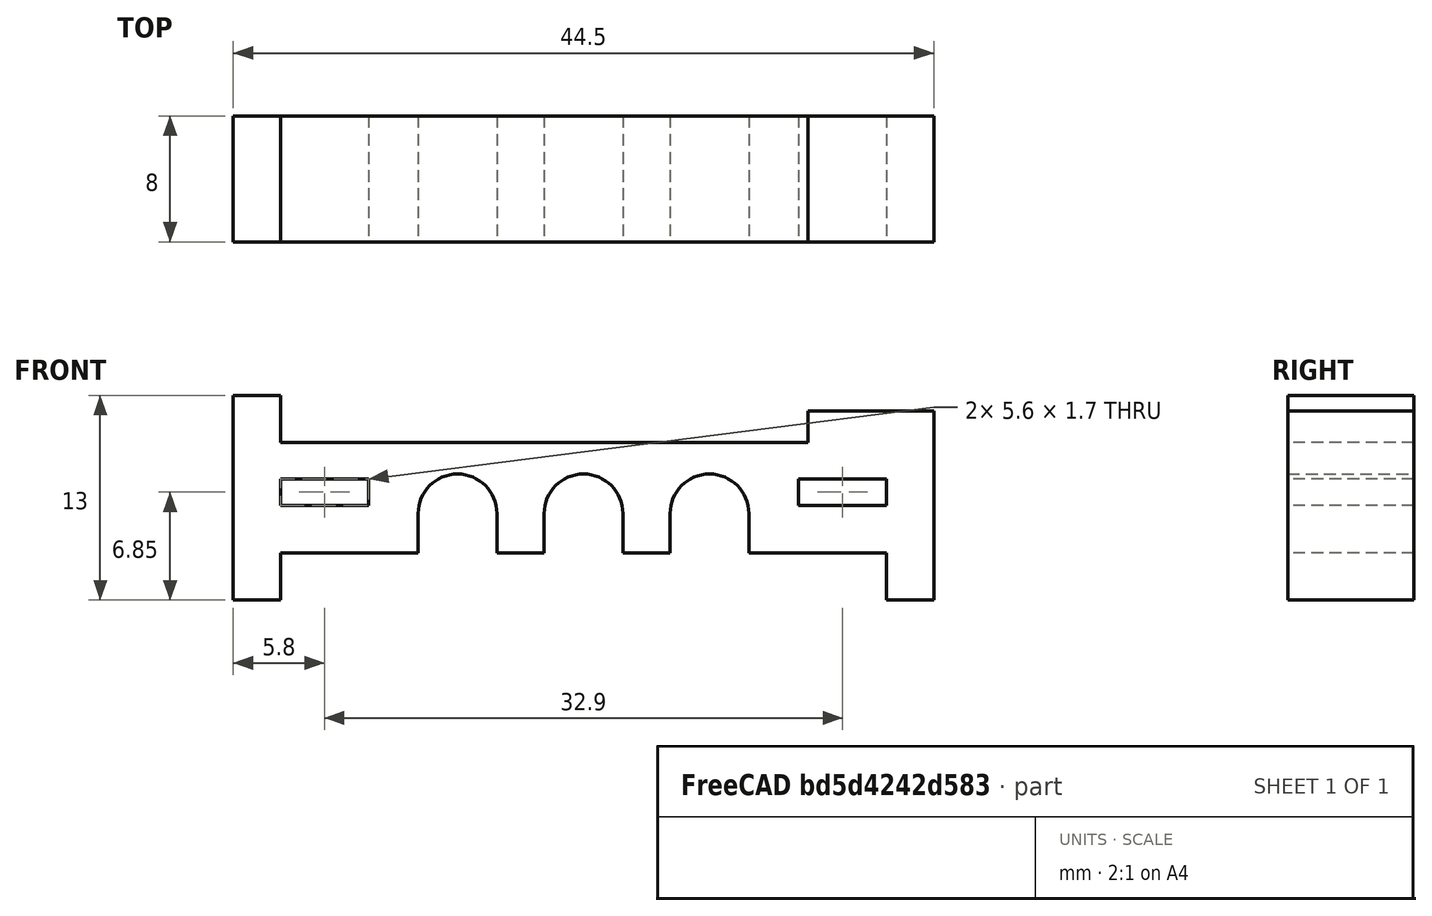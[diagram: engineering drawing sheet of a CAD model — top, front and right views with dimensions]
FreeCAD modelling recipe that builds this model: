
FCSTD DOCUMENT  (FreeCAD 0.19R24366 (Git))
Label: soundsupport
License: All rights reserved
LicenseURL: http://en.wikipedia.org/wiki/All_rights_reserved
objects: Sketcher::SketchObject×2, PartDesign::Pad×1, PartDesign::Body×1, Part::Part2DObjectPython×1
note: 6 computed .brp shape members not serialized (recipe doc carries the construction recipe); baked Part::Feature solids carry a one-line shape summary decoded from their .brp

FEATURE [Sketcher::SketchObject] Sketch
  FullyConstrained = true
  MapMode = 5
  Placement = pos=(0,0,0) rot=(1,0,0;1.5708rad)
  Support = -> [XZ_Plane]
  expr: Constraints[71] = .Constraints.radius
  sketch-geometry (32):
    g0: LineSegment StartX=-22.25 StartY=-3 StartZ=0 EndX=-19.25 EndY=-3 EndZ=0
    g1: LineSegment StartX=-19.25 StartY=-3 StartZ=0 EndX=-19.25 EndY=0 EndZ=0
    g2: LineSegment StartX=-19.25 StartY=0 StartZ=0 EndX=-10.5 EndY=0 EndZ=0
    g3: LineSegment StartX=-10.5 StartY=0 StartZ=0 EndX=-10.5 EndY=2.5 EndZ=0
    g4: LineSegment StartX=-5.5 StartY=2.5 StartZ=0 EndX=-5.5 EndY=0 EndZ=0
    g5: LineSegment StartX=-5.5 StartY=0 StartZ=0 EndX=-2.5 EndY=0 EndZ=0
    g6: LineSegment StartX=-2.5 StartY=0 StartZ=0 EndX=-2.5 EndY=2.5 EndZ=0
    g7: LineSegment StartX=2.5 StartY=2.5 StartZ=0 EndX=2.5 EndY=0 EndZ=0
    g8: LineSegment StartX=2.5 StartY=0 StartZ=0 EndX=5.5 EndY=0 EndZ=0
    g9: LineSegment StartX=5.5 StartY=0 StartZ=0 EndX=5.5 EndY=2.5 EndZ=0
    g10: LineSegment StartX=10.5 StartY=2.5 StartZ=0 EndX=10.5 EndY=0 EndZ=0
    g11: LineSegment StartX=10.5 StartY=0 StartZ=0 EndX=19.25 EndY=0 EndZ=0
    g12: LineSegment StartX=19.25 StartY=0 StartZ=0 EndX=19.25 EndY=-3 EndZ=0
    g13: LineSegment StartX=19.25 StartY=-3 StartZ=0 EndX=22.25 EndY=-3 EndZ=0
    g14: LineSegment StartX=22.25 StartY=-3 StartZ=0 EndX=22.25 EndY=9 EndZ=0
    g15: LineSegment StartX=22.25 StartY=9 StartZ=0 EndX=14.25 EndY=9 EndZ=0
    g16: LineSegment StartX=14.25 StartY=9 StartZ=0 EndX=14.25 EndY=7 EndZ=0
    g17: LineSegment StartX=14.25 StartY=7 StartZ=0 EndX=-19.25 EndY=7 EndZ=0
    g18: LineSegment StartX=-19.25 StartY=7 StartZ=0 EndX=-19.25 EndY=10 EndZ=0
    g19: LineSegment StartX=-19.25 StartY=10 StartZ=0 EndX=-22.25 EndY=10 EndZ=0
    g20: LineSegment StartX=-22.25 StartY=10 StartZ=0 EndX=-22.25 EndY=-3 EndZ=0
    g21: ArcOfCircle CenterX=-8 CenterY=2.5 CenterZ=0 NormalX=0 NormalY=0 NormalZ=1 AngleXU=0 Radius=2.5 StartAngle=3.48467e-08 EndAngle=3.14159
    g22: ArcOfCircle CenterX=-1.3e-15 CenterY=2.5 CenterZ=0 NormalX=0 NormalY=0 NormalZ=1 AngleXU=0 Radius=2.5 StartAngle=8.31012e-09 EndAngle=3.14159
    g23: ArcOfCircle CenterX=8 CenterY=2.5 CenterZ=0 NormalX=0 NormalY=0 NormalZ=1 AngleXU=0 Radius=2.5 StartAngle=6.28319 EndAngle=9.42478
    g24: LineSegment StartX=-19.25 StartY=4.7 StartZ=0 EndX=-13.65 EndY=4.7 EndZ=0
    g25: LineSegment StartX=-13.65 StartY=4.7 StartZ=0 EndX=-13.65 EndY=3 EndZ=0
    g26: LineSegment StartX=-13.65 StartY=3 StartZ=0 EndX=-19.25 EndY=3 EndZ=0
    g27: LineSegment StartX=-19.25 StartY=3 StartZ=0 EndX=-19.25 EndY=4.7 EndZ=0
    g28: LineSegment StartX=13.65 StartY=4.7 StartZ=0 EndX=19.25 EndY=4.7 EndZ=0
    g29: LineSegment StartX=19.25 StartY=4.7 StartZ=0 EndX=19.25 EndY=3 EndZ=0
    g30: LineSegment StartX=19.25 StartY=3 StartZ=0 EndX=13.65 EndY=3 EndZ=0
    g31: LineSegment StartX=13.65 StartY=3 StartZ=0 EndX=13.65 EndY=4.7 EndZ=0
  constraints (98):
    c: Horizontal(g0)
    c: Coincident(g0,g1)
    c: Vertical(g1)
    c: Coincident(g1,g2)
    c: Horizontal(g2)
    c: Coincident(g2,g3)
    c: Vertical(g3)
    c: Vertical(g4)
    c: Coincident(g4,g5)
    c: Horizontal(g5)
    c: Coincident(g5,g6)
    c: Vertical(g6)
    c: Vertical(g7)
    c: Coincident(g7,g8)
    c: Horizontal(g8)
    c: Coincident(g8,g9)
    c: Vertical(g9)
    c: Vertical(g10)
    c: Coincident(g10,g11)
    c: Horizontal(g11)
    c: Coincident(g11,g12)
    c: Vertical(g12)
    c: Coincident(g12,g13)
    c: Horizontal(g13)
    c: Coincident(g13,g14)
    c: Vertical(g14)
    c: Coincident(g14,g15)
    c: Horizontal(g15)
    c: Coincident(g15,g16)
    c: Coincident(g16,g17)
    c: Horizontal(g17)
    c: Coincident(g17,g18)
    c: Vertical(g18)
    c: Coincident(g18,g19)
    c: Horizontal(g19)
    c: Coincident(g19,g20)
    c: Coincident(g20,g0)
    c: Vertical(g20)
    c: Vertical(g16)
    c: Equal(g0,g1)
    c: Equal(g1,g12)
    c: Equal(g12,g13)
    c: DistanceX(g0,g0) = 3
    c: Equal(g3,g4)
    c: Equal(g4,g6)
    c: Equal(g6,g7)
    c: Equal(g7,g9)
    c: Equal(g9,g10)
    c: DistanceY(g3,g3) = 2.5  'radius'
    c: DistanceX(g17,g17) = 33.5
    c: DistanceX(g15,g15) = 8
    c: DistanceY(g16,g16) = 2
    c: DistanceY(g18,g18) = 3
    c: DistanceY(g11,g14) = 9
    c: Horizontal(g0,g12)
    c: Horizontal(g4,g2)
    c: Horizontal(g7,g10)
    c: Equal(g18,g19)
    c: Equal(g5,g8)
    c: DistanceX(g5,g5) = 3
    c: Coincident(g21,g4)
    c: Coincident(g21,g3)
    c: Coincident(g22,g7)
    c: Coincident(g22,g6)
    c: Coincident(g23,g10)
    c: Coincident(g23,g9)
    c: Tangent(g21,g3)
    c: Tangent(g22,g6)
    c: Tangent(g23,g9)
    c: Equal(g21,g22)
    c: Equal(g22,g23)
    c: Radius(g21) = 2.5
    c: Equal(g2,g11)
    c: Symmetric(g11,g1,g-1)
    c: Coincident(g24,g25)
    c: Coincident(g25,g26)
    c: Coincident(g26,g27)
    c: Coincident(g27,g24)
    c: Horizontal(g24)
    c: Horizontal(g26)
    c: Vertical(g25)
    c: Vertical(g27)
    c: Coincident(g28,g29)
    c: Coincident(g29,g30)
    c: Coincident(g30,g31)
    c: Coincident(g31,g28)
    c: Horizontal(g28)
    c: Horizontal(g30)
    c: Vertical(g29)
    c: Vertical(g31)
    c: Equal(g27,g31)
    c: Equal(g24,g28)
    c: DistanceY(g27,g27) = 1.7
    c: DistanceX(g24,g24) = 5.6
    c: Vertical(g1,g26)
    c: Vertical(g11,g29)
    c: DistanceY(g1,g26) = 3
    c: Horizontal(g30,g25)
FEATURE [PartDesign::Pad] Pad
  Direction = (1,1,1)
  Length = 8
  Length2 = 100
  Placement = pos=(0,0,0) rot=(1,0,0;1.5708rad)
  Profile = -> Sketch
  Refine = true
  Type = 0
FEATURE [PartDesign::Body] Body
  Group = -> [Sketch,Pad]
  Origin = -> Origin
  Tip = -> Pad
FEATURE [Part::Part2DObjectPython] Shape2DView  # Draft 2D object (typed FeaturePython)
  Base = -> Pad
  FaceNumbers = [33]
  FuseArch = false
  HiddenLines = false
  InPlace = true
  Projection = (0,-1,0)
  ProjectionMode = 0
  SegmentLength = 0.05
  Tessellation = false
  VisibleOnly = false
FEATURE [Sketcher::SketchObject] Sketch001  label="soundsupport"
  FullyConstrained = false
  sketch-geometry (32):
    g0: LineSegment StartX=-2.5 StartY=10.5 StartZ=0 EndX=-4.9e-15 EndY=10.5 EndZ=0
    g1: LineSegment StartX=-5.3e-15 StartY=10.5 StartZ=0 EndX=-5.3e-15 EndY=19.25 EndZ=0
    g2: LineSegment StartX=-5.3e-15 StartY=19.25 StartZ=0 EndX=3 EndY=19.25 EndZ=0
    g3: LineSegment StartX=3 StartY=19.25 StartZ=0 EndX=3 EndY=22.25 EndZ=0
    g4: LineSegment StartX=3 StartY=22.25 StartZ=0 EndX=-9 EndY=22.25 EndZ=0
    g5: LineSegment StartX=-9 StartY=22.25 StartZ=0 EndX=-9 EndY=14.25 EndZ=0
    g6: LineSegment StartX=-9 StartY=14.25 StartZ=0 EndX=-7 EndY=14.25 EndZ=0
    g7: LineSegment StartX=-7 StartY=14.25 StartZ=0 EndX=-7 EndY=-19.25 EndZ=0
    g8: LineSegment StartX=-7 StartY=-19.25 StartZ=0 EndX=-10 EndY=-19.25 EndZ=0
    g9: LineSegment StartX=-10 StartY=-19.25 StartZ=0 EndX=-10 EndY=-22.25 EndZ=0
    g10: LineSegment StartX=-10 StartY=-22.25 StartZ=0 EndX=3 EndY=-22.25 EndZ=0
    g11: LineSegment StartX=3 StartY=-22.25 StartZ=0 EndX=3 EndY=-19.25 EndZ=0
    g12: LineSegment StartX=3 StartY=-19.25 StartZ=0 EndX=-5.8e-15 EndY=-19.25 EndZ=0
    g13: LineSegment StartX=-5.3e-15 StartY=-19.25 StartZ=0 EndX=-5.3e-15 EndY=-10.5 EndZ=0
    g14: LineSegment StartX=-5.3e-15 StartY=-10.5 StartZ=0 EndX=-2.5 EndY=-10.5 EndZ=0
    g15: ArcOfCircle CenterX=-2.5 CenterY=-8 CenterZ=0 NormalX=0 NormalY=0 NormalZ=1 AngleXU=1.5708 Radius=2.5 StartAngle=3.48467e-08 EndAngle=3.14159
    g16: LineSegment StartX=-2.5 StartY=-5.5 StartZ=0 EndX=-4.9e-15 EndY=-5.5 EndZ=0
    g17: LineSegment StartX=-5.3e-15 StartY=-5.5 StartZ=0 EndX=-5.3e-15 EndY=-2.5 EndZ=0
    g18: LineSegment StartX=-5.3e-15 StartY=-2.5 StartZ=0 EndX=-2.5 EndY=-2.5 EndZ=0
    g19: ArcOfCircle CenterX=-2.5 CenterY=-1.3e-15 CenterZ=0 NormalX=0 NormalY=0 NormalZ=1 AngleXU=1.5708 Radius=2.5 StartAngle=8.31012e-09 EndAngle=3.14159
    g20: LineSegment StartX=-2.5 StartY=2.5 StartZ=0 EndX=-4.9e-15 EndY=2.5 EndZ=0
    g21: LineSegment StartX=-5.3e-15 StartY=2.5 StartZ=0 EndX=-5.3e-15 EndY=5.5 EndZ=0
    g22: LineSegment StartX=-5.3e-15 StartY=5.5 StartZ=0 EndX=-2.5 EndY=5.5 EndZ=0
    g23: ArcOfCircle CenterX=-2.5 CenterY=8 CenterZ=0 NormalX=0 NormalY=0 NormalZ=1 AngleXU=1.5708 Radius=2.5 StartAngle=6.28319 EndAngle=9.42478
    g24: LineSegment StartX=-4.7 StartY=13.65 StartZ=0 EndX=-4.7 EndY=19.25 EndZ=0
    g25: LineSegment StartX=-4.7 StartY=19.25 StartZ=0 EndX=-3 EndY=19.25 EndZ=0
    g26: LineSegment StartX=-3 StartY=19.25 StartZ=0 EndX=-3 EndY=13.65 EndZ=0
    g27: LineSegment StartX=-3 StartY=13.65 StartZ=0 EndX=-4.7 EndY=13.65 EndZ=0
    g28: LineSegment StartX=-4.7 StartY=-19.25 StartZ=0 EndX=-4.7 EndY=-13.65 EndZ=0
    g29: LineSegment StartX=-4.7 StartY=-13.65 StartZ=0 EndX=-3 EndY=-13.65 EndZ=0
    g30: LineSegment StartX=-3 StartY=-13.65 StartZ=0 EndX=-3 EndY=-19.25 EndZ=0
    g31: LineSegment StartX=-3 StartY=-19.25 StartZ=0 EndX=-4.7 EndY=-19.25 EndZ=0
